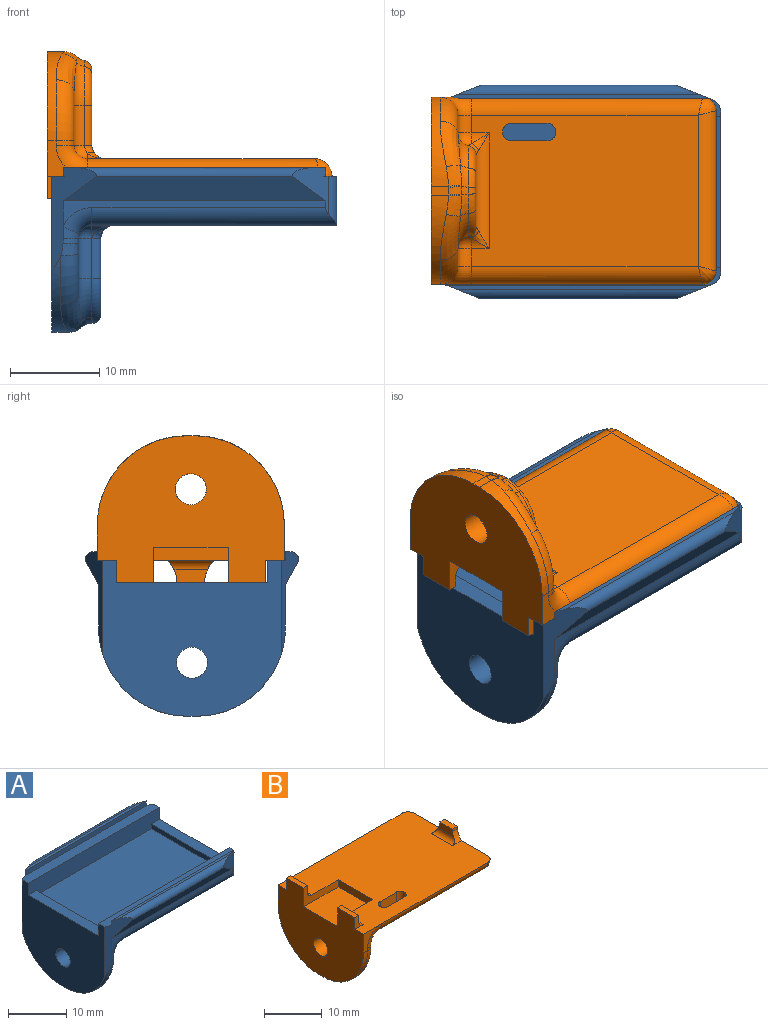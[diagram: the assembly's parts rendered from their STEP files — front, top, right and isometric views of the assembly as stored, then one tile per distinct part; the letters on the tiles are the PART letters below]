
ASSEMBLY  parts=2 mates=1
PART A: 82 faces, bbox 33.5x25.1x20.6 mm
  f0: plane 5.98x2.19mm, normal (1,0,0), area 8.3mm2, adj f1,f77,f78,f79,f80,f81
  f1: torus R=8mm, axis (1,0,0), area 17.9mm2, adj f0,f2,f76,f81
  f2: cylinder r=10mm len=9.9mm, axis (1,0,0), area 17.3mm2, adj f1,f3,f73,f74,f75,f76
  f3: plane 20x17.5mm, normal (-1,0,0), area 262.9mm2, adj f2,f4,f66,f67,f68,f69,f70,f71
  f4: plane 32x2mm, normal (0,0,1), area 63.2mm2, adj f3,f5,f59,f60,f61,f66,f75
  f5: plane 29.5x1mm, normal (0,-1,0), area 29.5mm2, adj f4,f6,f59,f75
  f6: plane 29.5x0.5mm, normal (0,0,1), area 14.1mm2, adj f5,f7,f59,f75
  f7: cylinder r=1mm len=27mm, axis (1,0,0), area 38.5mm2, adj f6,f8,f59,f75
  f8: plane 29.5x2.75mm, normal (0,0.88,-0.48), area 80.7mm2, adj f7,f9,f59,f75
  f9: plane 29.5x2.95mm, normal (0,1,0), area 24.1mm2, adj f8,f10,f12,f59,f75
  f10: torus R=3.5mm, axis (0,-1,0), area 8.3mm2, adj f9,f11,f12,f79
  f11: bspline ~2.17x1.94mm, area 2.4mm2, adj f10,f75,f79,f80
  f12: cylinder r=2mm len=27.5mm, axis (-1,0,0), area 84.7mm2, adj f9,f10,f13,f59,f60,f61
  f13: plane 27.5x17mm, normal (0,0,-1), area 435mm2, adj f12,f14,f54,f56,f57,f58,f61,f79
  f14: cylinder r=1.5mm len=2.5mm, axis (1,0,0), area 2.9mm2, adj f13,f15,f53
  f15: bspline ~2.5x2.5mm, area 1.6mm2, adj f14,f16,f54
  f16: cylinder r=1mm len=4.5mm, axis (0,0,-1), area 7.1mm2, adj f15,f17,f45,f78
  f17: torus R=4mm, axis (1,0,0), area 22.9mm2, adj f16,f18,f42,f43,f45,f77
  f18: cylinder r=5mm len=5.08mm, axis (-1,0,0), area 0.2mm2, adj f17,f19,f40,f41
  f19: bspline ~1.77x1.44mm, area 1mm2, adj f18,f20,f40,f41
  f20: bspline ~1.43x1.32mm, area 1.3mm2, adj f19,f21,f22,f73
  f21: bspline ~1.65x1.55mm, area 0.2mm2, adj f20,f41,f73,f74
  f22: bspline ~1.44x1.14mm, area 0.2mm2, adj f20,f23,f40,f73
  f23: bspline ~3.43x1.75mm, area 4mm2, adj f22,f24,f40,f71
  f24: bspline ~6.66x5.6mm, area 13.8mm2, adj f23,f25,f42,f71
  f25: torus R=8mm, axis (1,0,0), area 17.9mm2, adj f24,f26,f39,f71
  f26: plane 5.98x2.19mm, normal (1,0,0), area 8.3mm2, adj f25,f27,f29,f39,f42,f57
  f27: cylinder r=1.5mm len=4.5mm, axis (0,0,-1), area 10.6mm2, adj f26,f28,f42,f43
  f28: sphere r=1.5mm, area 4.8mm2, adj f27,f56,f57
  f29: cylinder r=2mm len=1.98mm, axis (0,0,-1), area 1.4mm2, adj f26,f30,f39,f70
  f30: bspline ~2.17x1.94mm, area 2.4mm2, adj f29,f31,f57,f70
  f31: torus R=3.5mm, axis (0,-1,0), area 8.3mm2, adj f30,f32,f57,f58
  f32: plane 29.5x2.95mm, normal (0,-1,0), area 24.1mm2, adj f31,f33,f37,f58,f70
  f33: plane 29.5x2.75mm, normal (0,-0.88,-0.48), area 80.7mm2, adj f32,f34,f37,f70
  f34: cylinder r=1mm len=27mm, axis (1,0,0), area 38.5mm2, adj f33,f35,f37,f70
  f35: plane 29.5x0.5mm, normal (0,0,1), area 14.1mm2, adj f34,f36,f37,f70
  f36: plane 29.5x1mm, normal (0,1,0), area 29.5mm2, adj f35,f37,f69,f70
  f37: plane 6.24x5.11mm, normal (0.37,-0.93,0), area 10.3mm2, adj f32,f33,f34,f35,f36,f38,f58,f69
  f38: cylinder r=1.5mm len=5.44mm, axis (0,0,-1), area 8.6mm2, adj f37,f58,f61,f69
  f39: bspline ~2.2x2.15mm, area 3.9mm2, adj f25,f26,f29,f70
  f40: bspline ~4.6x2.02mm, area 3mm2, adj f18,f19,f22,f23,f42
  f41: bspline ~4.12x1.98mm, area 3mm2, adj f18,f19,f21,f74,f77
  f42: torus R=6.5mm, axis (1,0,0), area 11.2mm2, adj f17,f24,f26,f27,f40
  f43: cylinder r=1mm len=4.5mm, axis (0,0,1), area 7.1mm2, adj f17,f27,f44,f45
  f44: bspline ~1.59x1.59mm, area 0.8mm2, adj f43,f54,f56
  f45: plane 8.5x8mm, normal (1,0,0), area 34.9mm2, adj f16,f17,f43,f46,f48,f49,f50,f51
  f46: plane 2.75x2.5mm, normal (0,0.87,0.5), area 7.9mm2, adj f45,f47,f48,f52
  f47: plane 6.35x5.5mm, normal (1,0,0), area 16.6mm2, adj f46,f48,f49,f50,f51,f52,f72
  f48: plane 3.18x2.5mm, normal (0,0,1), area 7.9mm2, adj f45,f46,f47,f49
  f49: plane 2.75x2.5mm, normal (0,-0.87,0.5), area 7.9mm2, adj f45,f47,f48,f50
  f50: plane 2.75x2.5mm, normal (0,-0.87,-0.5), area 7.9mm2, adj f45,f47,f49,f51
  f51: plane 3.18x2.5mm, normal (0,0,-1), area 7.9mm2, adj f45,f47,f50,f52
  f52: plane 2.75x2.5mm, normal (0,0.87,-0.5), area 7.9mm2, adj f45,f46,f47,f51
  f53: sphere r=1.5mm, area 3.5mm2, adj f14,f78,f79
  f54: cylinder r=1.5mm len=13mm, axis (0,1,0), area 24.7mm2, adj f13,f15,f44,f45,f55
  f55: bspline ~1.83x1.83mm, area 0.3mm2, adj f54,f56
  f56: cylinder r=1.5mm len=2.5mm, axis (-1,0,0), area 2.9mm2, adj f13,f28,f44,f55
  f57: cylinder r=1.5mm len=2.02mm, axis (0,1,0), area 4.7mm2, adj f13,f26,f28,f30,f31
  f58: cylinder r=2mm len=27.5mm, axis (1,0,0), area 84.7mm2, adj f13,f31,f32,f37,f38,f61
  f59: plane 6.24x5.11mm, normal (0.37,0.93,0), area 10.3mm2, adj f4,f5,f6,f7,f8,f9,f12,f60
  f60: cylinder r=1.5mm len=5.44mm, axis (0,0,1), area 8.6mm2, adj f4,f12,f59,f61
  f61: plane 17.97x5.5mm, normal (1,0,0), area 56.3mm2, adj f4,f12,f13,f38,f58,f60,f62,f66
  f62: plane 17x2mm, normal (0,0,1), area 34mm2, adj f61,f63,f66,f68
  f63: plane 17x1mm, normal (-1,0,0), area 17mm2, adj f62,f64,f66,f68
  f64: plane 28x17mm, normal (0,0,1), area 476mm2, adj f63,f65,f66,f68
  f65: plane 17x1mm, normal (1,0,0), area 17mm2, adj f64,f66,f67,f68
  f66: plane 32x3.5mm, normal (0,-1,0), area 108mm2, adj f3,f4,f61,f62,f63,f64,f65,f67
  f67: plane 17x2mm, normal (0,0,1), area 34mm2, adj f3,f65,f66,f68
  f68: plane 32x3.5mm, normal (0,1,0), area 108mm2, adj f3,f61,f62,f63,f64,f65,f67,f69
  f69: plane 32x2mm, normal (0,0,1), area 63.2mm2, adj f3,f36,f37,f38,f61,f68,f70
  f70: plane 12.67x6.05mm, normal (-0.37,-0.93,0), area 21.9mm2, adj f3,f29,f30,f32,f33,f34,f35,f36
  f71: cylinder r=10mm len=9.9mm, axis (-1,0,0), area 17.3mm2, adj f3,f23,f24,f25,f70,f73
  f72: cylinder r=1.75mm len=3.5mm, axis (-1,0,0), area 33mm2, adj f3,f47
  f73: plane 1.96x1mm, normal (0,0,-1), area 2mm2, adj f2,f3,f20,f21,f22,f71
  f74: bspline ~3.34x1.73mm, area 4mm2, adj f2,f21,f41,f76
  f75: plane 12.67x6.05mm, normal (-0.37,0.93,0), area 21.9mm2, adj f2,f3,f4,f5,f6,f7,f8,f9
  f76: bspline ~6.8x5.63mm, area 13.8mm2, adj f1,f2,f74,f77
  f77: torus R=6.5mm, axis (1,0,0), area 11.2mm2, adj f0,f17,f41,f76,f78
  f78: cylinder r=1.5mm len=4.5mm, axis (0,0,1), area 10.6mm2, adj f0,f16,f53,f77
  f79: cylinder r=1.5mm len=2.02mm, axis (0,1,0), area 4.7mm2, adj f0,f10,f11,f13,f53
  f80: cylinder r=2mm len=1.98mm, axis (0,0,-1), area 1.4mm2, adj f0,f11,f75,f81
  f81: bspline ~2.13x2.13mm, area 3.9mm2, adj f0,f1,f75,f80
PART B: 86 faces, bbox 32.9x22.7x17.6 mm
  f0: plane 5.98x2.17mm, normal (1,0,0), area 8.3mm2, adj f39,f40,f41,f56,f58
  f1: cylinder r=1.75mm len=3.5mm, axis (-1,0,0), area 27.5mm2, adj f5,f32
  f2: plane 25.5x17mm, normal (0,0,-1), area 396.4mm2, adj f39,f44,f46,f48,f49,f62,f66,f70
  f3: plane 5.98x2.17mm, normal (1,0,0), area 8.3mm2, adj f48,f50,f52,f65,f67
  f4: plane 32.05x21.05mm, normal (0,0,1), area 560.3mm2, adj f5,f8,f9,f10,f11,f12,f14,f16
  f5: plane 21x16.5mm, normal (-1,0,0), area 249.9mm2, adj f1,f4,f8,f9,f12,f14,f16,f17
  f6: plane 5.16x2.5mm, normal (1,0,0), area 9.4mm2, adj f10,f11,f22,f23,f24,f66
  f7: plane 3.79x1.5mm, normal (-1,0,0), area 5mm2, adj f10,f11,f22,f23,f24,f27
  f8: plane 4.5x4mm, normal (0,-1,0), area 6.6mm2, adj f4,f5,f29,f67,f69
  f9: plane 4.5x4mm, normal (0,1,0), area 6.6mm2, adj f4,f5,f30,f58,f60
  f10: cylinder r=3.99mm len=2.2mm, axis (1,0,0), area 3.3mm2, adj f4,f6,f7,f23,f27
  f11: cylinder r=3.99mm len=2.2mm, axis (1,0,0), area 3.3mm2, adj f4,f6,f7,f22,f27
  f12: plane 8.5x4mm, normal (0,-1,0), area 15.5mm2, adj f4,f5,f13,f18,f19,f20,f26
  f13: plane 4.2x1.5mm, normal (1,0,0), area 6.3mm2, adj f12,f14,f20,f26
  f14: plane 2.5x2mm, normal (0,1,0), area 2.7mm2, adj f4,f5,f13,f20,f26
  f15: plane 4.2x1.5mm, normal (1,0,0), area 6.3mm2, adj f16,f17,f21,f25
  f16: plane 8.5x4mm, normal (0,1,0), area 15.5mm2, adj f4,f5,f15,f18,f19,f21,f25
  f17: plane 2.5x2mm, normal (0,-1,0), area 2.7mm2, adj f4,f5,f15,f21,f25
  f18: plane 8.4x1.5mm, normal (-1,0,0), area 12.6mm2, adj f4,f12,f16,f19
  f19: plane 8.5x8.4mm, normal (0,0,1), area 71.4mm2, adj f5,f12,f16,f18
  f20: plane 4.2x1mm, normal (0,0,1), area 4.2mm2, adj f5,f12,f13,f14
  f21: plane 4.2x1mm, normal (0,0,1), area 4.2mm2, adj f5,f15,f16,f17
  f22: plane 1.2x0.5mm, normal (0,-1,0), area 0.6mm2, adj f6,f7,f11,f24
  f23: plane 1.2x0.5mm, normal (0,1,0), area 0.6mm2, adj f6,f7,f10,f24
  f24: plane 3.14x1.2mm, normal (0,0,1), area 3.8mm2, adj f6,f7,f22,f23
  f25: cylinder r=1mm len=4.2mm, axis (0,1,0), area 6.6mm2, adj f4,f15,f16,f17
  f26: cylinder r=1mm len=4.2mm, axis (0,1,0), area 6.6mm2, adj f4,f12,f13,f14
  f27: cylinder r=1mm len=5.16mm, axis (0,-1,0), area 7mm2, adj f4,f7,f10,f11
  f28: plane 1.96x1mm, normal (0,0,-1), area 2mm2, adj f5,f29,f30,f55,f57,f59
  f29: cylinder r=10mm len=10mm, axis (-1,0,0), area 19.5mm2, adj f5,f8,f28,f61,f63,f65
  f30: cylinder r=10mm len=10mm, axis (1,0,0), area 19.5mm2, adj f5,f9,f28,f53,f54,f56
  f31: plane 8.54x8.1mm, normal (1,0,0), area 36mm2, adj f33,f34,f35,f36,f37,f38,f46,f73
  f32: plane 6.35x5.5mm, normal (1,0,0), area 16.6mm2, adj f1,f33,f34,f35,f36,f37,f38
  f33: plane 2.75x2.5mm, normal (0,0.87,0.5), area 7.9mm2, adj f31,f32,f34,f38
  f34: plane 3.18x2.5mm, normal (0,0,1), area 7.9mm2, adj f31,f32,f33,f35
  f35: plane 2.75x2.5mm, normal (0,-0.87,0.5), area 7.9mm2, adj f31,f32,f34,f36
  f36: plane 2.75x2.5mm, normal (0,-0.87,-0.5), area 7.9mm2, adj f31,f32,f35,f37
  f37: plane 3.18x2.5mm, normal (0,0,-1), area 7.9mm2, adj f31,f32,f36,f38
  f38: plane 2.75x2.5mm, normal (0,0.87,-0.5), area 7.9mm2, adj f31,f32,f33,f37
  f39: cylinder r=1.5mm len=2mm, axis (0,1,0), area 4.7mm2, adj f0,f2,f42,f60
  f40: cylinder r=1.5mm len=4.5mm, axis (0,0,1), area 9.2mm2, adj f0,f41,f42,f73
  f41: torus R=6.5mm, axis (1,0,0), area 9.6mm2, adj f0,f40,f43,f54,f74
  f42: sphere r=1.5mm, area 3.4mm2, adj f39,f40,f44,f72
  f43: bspline ~4.12x1.98mm, area 2.3mm2, adj f41,f45,f53,f55,f75
  f44: cylinder r=1.5mm len=2mm, axis (1,0,0), area 1.4mm2, adj f2,f42,f71
  f45: bspline ~1.77x1.44mm, area 0.8mm2, adj f43,f47,f57,f76
  f46: cylinder r=1.5mm len=13mm, axis (0,1,0), area 23.6mm2, adj f2,f31,f71,f72,f80,f81
  f47: bspline ~4.6x2.02mm, area 2.3mm2, adj f45,f50,f59,f61,f77
  f48: cylinder r=1.5mm len=2mm, axis (0,1,0), area 4.7mm2, adj f2,f3,f51,f69
  f49: cylinder r=1.5mm len=2mm, axis (-1,0,0), area 1.4mm2, adj f2,f51,f80
  f50: torus R=6.5mm, axis (1,0,0), area 9.6mm2, adj f3,f47,f52,f63,f78
  f51: sphere r=1.5mm, area 3.4mm2, adj f48,f49,f52,f81
  f52: cylinder r=1.5mm len=4.5mm, axis (0,0,-1), area 9.2mm2, adj f3,f50,f51,f79
  f53: bspline ~3.34x1.73mm, area 4mm2, adj f30,f43,f54,f55
  f54: bspline ~8.32x5.78mm, area 13.8mm2, adj f30,f41,f53,f56
  f55: bspline ~1.95x1.64mm, area 0.2mm2, adj f28,f43,f53,f57
  f56: torus R=8mm, axis (1,0,0), area 22mm2, adj f0,f30,f54,f58
  f57: bspline ~1.43x1.32mm, area 1.3mm2, adj f28,f45,f55,f59
  f58: cylinder r=2mm len=2mm, axis (0,0,-1), area 1.6mm2, adj f0,f9,f56,f60
  f59: bspline ~2.05x1.55mm, area 0.2mm2, adj f28,f47,f57,f61
  f60: torus R=3.5mm, axis (0,-1,0), area 11mm2, adj f9,f39,f58,f62
  f61: bspline ~3.43x1.75mm, area 4mm2, adj f29,f47,f59,f63
  f62: cylinder r=2mm len=26mm, axis (-1,0,0), area 80.9mm2, adj f2,f4,f60,f64
  f63: bspline ~6.66x5.6mm, area 13.8mm2, adj f29,f50,f61,f65
  f64: bspline ~2.11x2mm, area 3.3mm2, adj f4,f62,f66
  f65: torus R=8mm, axis (1,0,0), area 22mm2, adj f3,f29,f63,f67
  f66: cylinder r=2mm len=18mm, axis (0,1,0), area 55mm2, adj f2,f4,f6,f64,f68
  f67: cylinder r=2mm len=2mm, axis (0,0,1), area 1.6mm2, adj f3,f8,f65,f69
  f68: bspline ~2.11x2mm, area 3.3mm2, adj f4,f66,f70
  f69: torus R=3.5mm, axis (0,-1,0), area 11mm2, adj f8,f48,f67,f70
  f70: cylinder r=2mm len=26mm, axis (1,0,0), area 80.9mm2, adj f2,f4,f68,f69
  f71: bspline ~2.12x2.12mm, area 0.9mm2, adj f44,f46,f72
  f72: bspline ~1.45x1.28mm, area 1.2mm2, adj f42,f46,f71,f73
  f73: cylinder r=1mm len=4.5mm, axis (0,0,1), area 6.2mm2, adj f31,f40,f72,f74
  f74: torus R=4.05mm, axis (-1,0,0), area 6.6mm2, adj f31,f41,f73,f75
  f75: bspline ~2.59x1.6mm, area 2.9mm2, adj f31,f43,f74,f76
  f76: bspline ~1.01x1mm, area 1mm2, adj f31,f45,f75,f77
  f77: bspline ~3x1.77mm, area 2.9mm2, adj f31,f47,f76,f78
  f78: torus R=4.05mm, axis (-1,0,0), area 6.6mm2, adj f31,f50,f77,f79
  f79: cylinder r=1mm len=4.5mm, axis (0,0,-1), area 6.2mm2, adj f31,f52,f78,f81
  f80: bspline ~2.12x2.12mm, area 0.9mm2, adj f46,f49,f81
  f81: bspline ~1.45x1.28mm, area 1.2mm2, adj f46,f51,f79,f80
  f82: cylinder r=1mm len=2mm, axis (0,0,-1), area 6.3mm2, adj f2,f4,f83,f84
  f83: plane 4x2mm, normal (0,1,0), area 8mm2, adj f2,f4,f82,f85
  f84: plane 4x2mm, normal (0,-1,0), area 8mm2, adj f2,f4,f82,f85
  f85: cylinder r=1mm len=2mm, axis (0,0,-1), area 6.3mm2, adj f2,f4,f83,f84
PLACE A t=(-4.09,-5.22,-5.56)mm fixed
PLACE B rot(axis=(1,0,0),180deg) t=(-1.01,-5.69,1.94)mm
MATE parallel A.f64 <-> B.f4  axis (0,0,1) through (-0.49,-5.82,-3.56)mm
